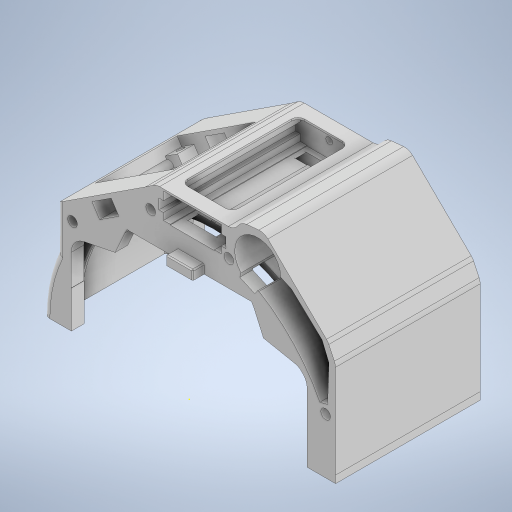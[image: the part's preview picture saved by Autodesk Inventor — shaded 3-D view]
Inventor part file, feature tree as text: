
AUTODESK INVENTOR PART (.ipt)
format: ipt  version: 2023.4 (Build 274418000, 418)  size: 1,504,256 bytes
history: native  units: mm
features: sketch x53, extrude x51, projected_geometry x31, thicken_offset x3, fillet x3, chamfer x3, plane x1
ambient origin geometry x8: Origin, YZ Plane, XZ Plane, XY Plane, X Axis, Y Axis, Z Axis, Center Point
bodies: Solid1 (feature_tree)
feature tree (145):
  extrude  "Extrusion1"  Depth=2.0mm
  extrude  "Extrusion2"  Depth=122.0mm
  extrude  "Extrusion3"  Depth=4.6mm TaperAngle=0.0deg
  extrude  "Extrusion4"  Depth=2.0mm TaperAngle=0.0deg
  extrude  "Extrusion5"  Depth=0.1mm
  thicken_offset  "Thicken1"
  thicken_offset  "Thicken2"
  extrude  "Extrusion6"  Depth=0.1mm
  extrude  "Extrusion7"  Depth=7.0mm TaperAngle=0.0deg
  extrude  "Extrusion8"  Depth=10.0mm TaperAngle=0.0deg
  extrude  "Extrusion9"  Depth=9.0mm TaperAngle=0.0deg
  extrude  "Extrusion10"  Depth=10.0mm TaperAngle=0.0deg
  extrude  "Extrusion11"  TaperAngle=0.0deg  [1 undecoded]
  extrude  "Extrusion12"  Depth=4.1mm TaperAngle=0.0deg
  extrude  "Extrusion51"  Depth=19.3mm
  extrude  "Extrusion52"  Depth=10.0mm
  extrude  "Extrusion53"  TaperAngle=0.0deg  [1 undecoded]
  extrude  "Extrusion54"  TaperAngle=0.0deg  [1 undecoded]
  extrude  "Extrusion55"  Depth=10.5mm TaperAngle=0.0deg
  extrude  "Extrusion56"  Depth=3.0mm TaperAngle=0.0deg
  extrude  "Extrusion57"  Depth=1.5mm
  extrude  "Extrusion58"  Depth=1.5mm
  sketch  "Sketch60"  dims[d192=3.6mm d193=2.0mm]
  extrude  "Extrusion59"  Depth=2.0mm
  extrude  "Extrusion60"  Depth=1.5mm TaperAngle=0.0deg
  extrude  "Extrusion61"  Depth=3.0mm
  extrude  "Extrusion62"  Depth=5.082328mm
  extrude  "Extrusion63"  TaperAngle=0.0deg  [1 undecoded]
  extrude  "Extrusion64"  Depth=40.8mm
  extrude  "Extrusion65"  Depth=4.85mm TaperAngle=0.0deg
  fillet  "Fillet3"  [1 undecoded]
  extrude  "Extrusion66"  Depth=3.25mm
  extrude  "Extrusion67"  Depth=3.25mm
  plane  "Work Plane3"
  extrude  "Extrusion68"  Depth=2.5mm
  extrude  "Extrusion69"  Depth=2.5mm
  extrude  "Extrusion70"  Depth=2.5mm
  extrude  "Extrusion71"  Depth=2.5mm
  sketch  "Sketch74"  dims[d230=10.0mm d231=0.0mm d233=0.0mm d234=0.0mm]
  extrude  "Extrusion72"  Depth=10.0mm TaperAngle=0.0deg
  fillet  "Fillet5"  Radius=10.0mm
  extrude  "Extrusion73"  TaperAngle=0.0deg  [1 undecoded]
  extrude  "Extrusion74"  Depth=10.0mm TaperAngle=0.0deg
  extrude  "Extrusion75"  Depth=2.0mm TaperAngle=0.0deg
  extrude  "Extrusion76"  TaperAngle=0.0deg  [1 undecoded]
  extrude  "Extrusion77"  Depth=0.2mm
  thicken_offset  "Thicken3"
  extrude  "Extrusion78"  Depth=0.7mm
  extrude  "Extrusion79"  Depth=0.6mm
  extrude  "Extrusion80"  Depth=10.0mm TaperAngle=0.0deg
  extrude  "Extrusion81"  Depth=12.0mm
  extrude  "Extrusion82"  Depth=4.0mm
  extrude  "Extrusion83"  Depth=5.0mm TaperAngle=0.0deg
  chamfer  "Chamfer12"  Distance=1.5mm
  chamfer  "Chamfer13"  Distance=1.5mm
  extrude  "Extrusion84"  Depth=1.5mm TaperAngle=45.0deg
  extrude  "Extrusion85"  Depth=0.3mm
  fillet  "Fillet6"  Radius=3.0mm
  chamfer  "Chamfer14"  Distance=10.0mm
  extrude  "Extrusion86"  Depth=3.0mm TaperAngle=45.0deg
  extrude  "Extrusion87"  Depth=4.3mm
  extrude  "Extrusion88"  Depth=4.3mm
  extrude  "Extrusion89"  Depth=3.0mm
  sketch  "Sketch1"  dims[d0=125.0mm d1=2.0mm]
  sketch  "Sketch2"  dims[d2=4.6mm d3=0.0mm d4=122.0mm]
  sketch  "Sketch3"  dims[d5=42.8mm d6=0.0mm d7=4.6mm d8=0.0mm]
  projected_geometry  "Projected Loop1"
  sketch  "Sketch4"  dims[d10=2.0mm d11=0.0mm d12=2.0mm d13=0.0mm]
  sketch  "Sketch5"  dims[d14=0.1mm d15=0.1mm]
  projected_geometry  "Projected Loop2"
  projected_geometry  "Projected Loop3"
  sketch  "Sketch6"  dims[d16=0.1mm d17=0.1mm]
  projected_geometry  "Projected Loop4"
  sketch  "Sketch7"  dims[d18=0.0mm d19=0.0mm d20=7.0mm d21=0.0mm]
  projected_geometry  "Projected Loop5"
  sketch  "Sketch8"  dims[d22=0.0mm d23=0.0mm d24=10.0mm d25=0.0mm]
  projected_geometry  "Projected Loop6"
  projected_geometry  "Projected Loop7"
  sketch  "Sketch9"  dims[d26=9.0mm d27=0.0mm d28=9.0mm d29=0.0mm]
  projected_geometry  "Projected Loop8"
  sketch  "Sketch10"  dims[d30=10.0mm d31=0.0mm d158=10.0mm d159=0.0mm]
  sketch  "Sketch11"  dims[d160=10.0mm d161=0.0mm d162=0.0mm d163=0.0mm]
  projected_geometry  "Projected Loop9"
  sketch  "Sketch12"  dims[d164=3.7mm d165=0.0mm d166=4.1mm d167=0.0mm]
  sketch  "Sketch52"  dims[d168=4.1mm d169=0.0mm d170=19.3mm]
  sketch  "Sketch53"  dims[d171=10.0mm d172=0.0mm d173=25.5mm]
  sketch  "Sketch54"  dims[d174=2.0mm d175=0.0mm d176=0.0mm]
  sketch  "Sketch55"  dims[d177=0.0mm d178=0.0mm]
  projected_geometry  "Projected Loop42"
  sketch  "Sketch56"  dims[d179=54.5mm d180=10.5mm d181=0.0mm]
  projected_geometry  "Projected Loop43"
  sketch  "Sketch57"  dims[d182=3.0mm d183=0.0mm d184=3.0mm d185=0.0mm]
  sketch  "Sketch58"  dims[d186=3.0mm d187=0.0mm d188=1.5mm]
  sketch  "Sketch59"  dims[d189=1.5mm d190=0.0mm d191=3.6mm]
  sketch  "Sketch61"  dims[d194=2.0mm d195=1.5mm d196=0.0mm]
  projected_geometry  "Projected Loop44"
  sketch  "Sketch62"  dims[d197=10.0mm d198=0.0mm d199=3.0mm]
  projected_geometry  "Projected Loop45"
  sketch  "Sketch63"  dims[d200=32.135893mm d202=5.082328mm]
  projected_geometry  "Projected Loop46"
  projected_geometry  "Projected Loop47"
  sketch  "Sketch64"  dims[d203=19.3mm d204=0.0mm d205=0.0mm]
  projected_geometry  "Projected Loop48"
  sketch  "Sketch65"  dims[d206=35.6mm d207=40.8mm]
  projected_geometry  "Projected Loop49"
  sketch  "Sketch66"  dims[d208=2.0mm d209=4.85mm d210=0.0mm d211=-1.65mm]
  sketch  "Sketch67"  dims[d212=3.25mm d213=3.25mm]
  projected_geometry  "Projected Loop50"
  sketch  "Sketch68"  dims[d214=3.25mm d215=3.25mm]
  sketch  "Sketch69"  dims[d216=2.5mm d217=2.5mm]
  projected_geometry  "Projected Loop51"
  sketch  "Sketch70"  dims[d218=2.5mm d219=2.5mm]
  projected_geometry  "Projected Loop52"
  sketch  "Sketch71"  dims[d220=2.5mm d221=2.5mm]
  sketch  "Sketch72"  dims[d222=2.5mm d223=2.5mm]
  projected_geometry  "Projected Loop53"
  sketch  "Sketch73"  dims[d224=4.85mm d225=0.0mm d226=10.0mm d227=0.0mm d228=10.0mm d229=0.0mm]
  projected_geometry  "Projected Loop54"
  sketch  "Sketch75"  dims[d235=5.0mm d236=10.0mm d237=0.0mm]
  sketch  "Sketch76"  dims[d238=1.0mm d239=0.0mm d240=2.0mm d241=0.0mm]
  sketch  "Sketch77"  dims[d242=2.0mm d243=0.0mm d244=0.0mm d245=0.0mm]
  projected_geometry  "Projected Loop55"
  sketch  "Sketch78"  dims[d246=0.2mm d247=0.2mm]
  projected_geometry  "Projected Loop56"
  sketch  "Sketch79"  dims[d248=0.6mm d249=0.7mm]
  projected_geometry  "Projected Loop57"
  sketch  "Sketch80"  dims[d250=0.6mm d251=0.6mm]
  sketch  "Sketch81"  dims[d252=0.6mm d253=10.0mm d254=0.0mm]
  projected_geometry  "Projected Loop58"
  sketch  "Sketch82"  dims[d255=0.0mm d256=0.0mm d257=12.0mm]
  sketch  "Sketch83"  dims[d258=22.0mm d259=4.0mm]
  sketch  "Sketch84"  dims[d260=5.0mm d261=0.0mm d262=5.0mm d263=0.0mm]
  sketch  "Sketch85"  dims[d264=1.5mm d265=1.5mm d266=0.0mm d267=1.5mm d268=0.0mm]
  sketch  "Sketch86"  dims[d269=1.5mm d270=2.0mm d271=45.0deg d272=0.5mm d273=2.0mm d274=45.0deg]
  projected_geometry  "Projected Loop59"
  projected_geometry  "Projected Loop60"
  sketch  "Sketch87"  dims[d275=0.0mm d276=0.0mm d277=0.3mm d278=3.0mm]
  sketch  "Sketch88"  dims[d279=3.0mm d280=10.0mm d281=0.0mm]
  sketch  "Sketch89"  dims[d282=3.0mm d283=0.5mm d284=2.0mm d285=45.0deg]
  projected_geometry  "Projected Loop61"
  sketch  "Sketch90"  dims[d286=4.3mm d287=4.3mm]
  sketch  "Sketch91"  dims[d288=4.3mm d289=4.3mm]
  projected_geometry  "Projected Loop62"
  sketch  "Sketch92"  dims[d290=0.0mm d291=0.0mm d292=3.0mm d293=10.0mm d294=0.0mm d295=1.0mm d296=0.0mm d297=0.0mm d298=0.0mm d9=0.5mm d36=0.5mm d37=0.872665mm d38=0.5mm d39=0.872665mm]
  projected_geometry  "Projected Loop63"
note: 7 required parameter values undecoded (feature->parameter linkage not recoverable at this tier; creation-order binding heuristic only, values carry confidence <= 0.55)
